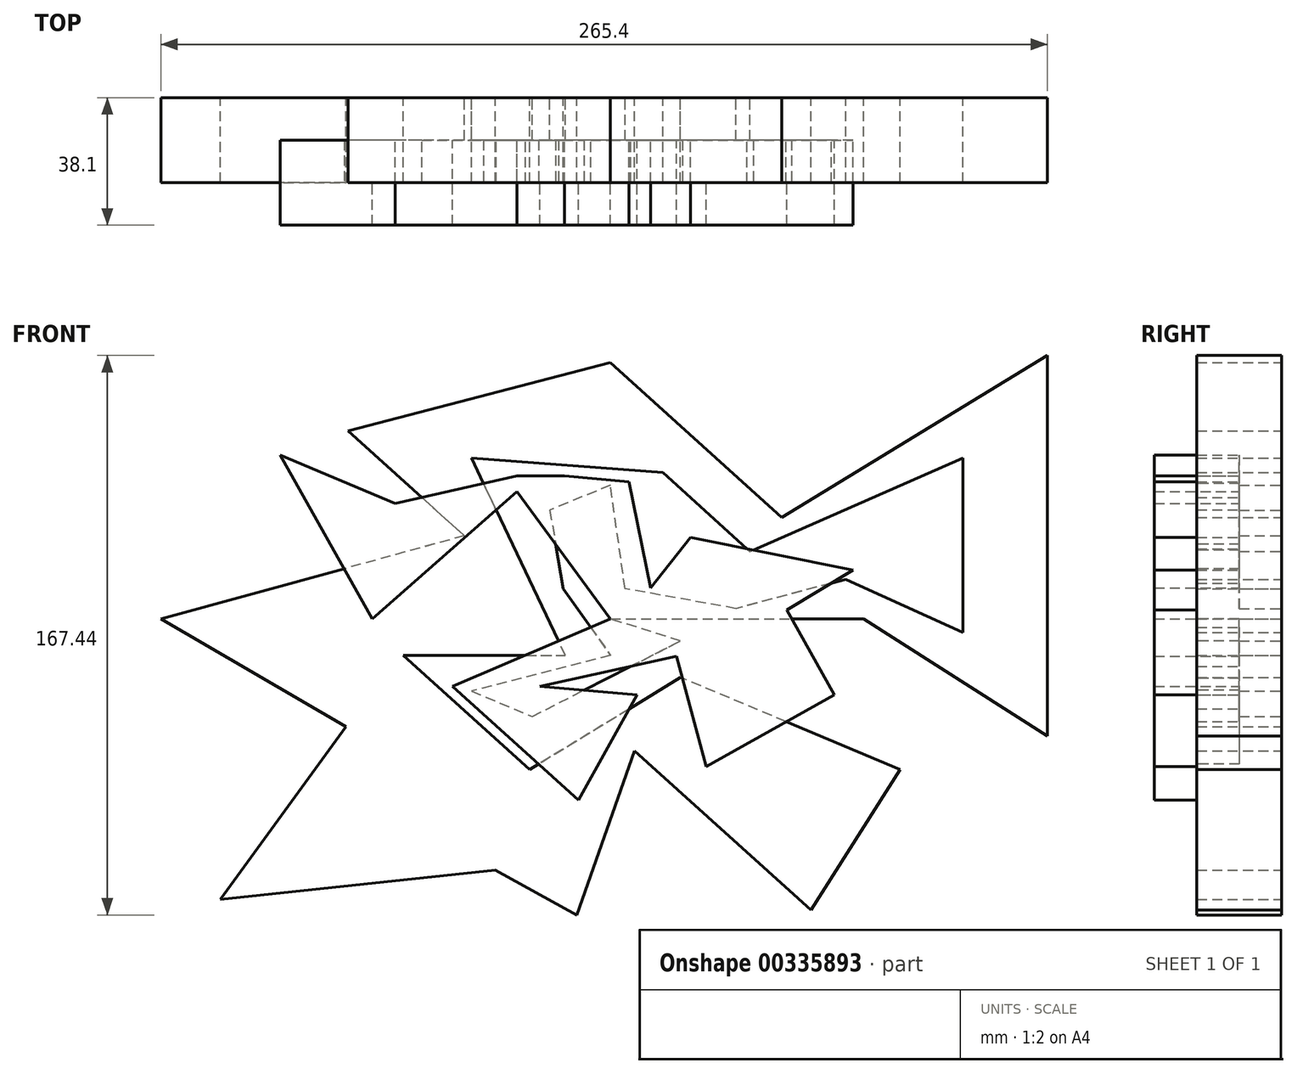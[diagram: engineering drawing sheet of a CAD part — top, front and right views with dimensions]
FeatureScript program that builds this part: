
annotation { "Feature Type Name" : "Feature", "Feature Type Description" : "" }
export const myFeature = defineFeature(function(context is Context, id is Id, definition is map)
    precondition{}
    {
        {
            var Q0;
            Q0=qCreatedBy(makeId("Front.planeOp"),FACE);
            var sketch = newSketch(context, id + "F0", { "sketchPlane" : qUnion([Q0])});
            skLineSegment(sketch, "E0", {"start": v(0, 0) * mm, "end": v(75.74, 0) * mm});
            skLineSegment(sketch, "E1", {"start": v(75.74, 0) * mm, "end": v(130.82, -35.05) * mm});
            skLineSegment(sketch, "E2", {"start": v(130.82, -35.05) * mm, "end": v(130.82, 78.87) * mm});
            skLineSegment(sketch, "E3", {"start": v(130.82, 78.87) * mm, "end": v(51.33, 30.36) * mm});
            skLineSegment(sketch, "E4", {"start": v(51.33, 30.36) * mm, "end": v(0, 76.68) * mm});
            skLineSegment(sketch, "E5", {"start": v(0, 76.68) * mm, "end": v(-78.56, 56.34) * mm});
            skLineSegment(sketch, "E6", {"start": v(-78.56, 56.34) * mm, "end": v(-43.72, 24.9) * mm});
            skLineSegment(sketch, "E7", {"start": v(-43.72, 24.9) * mm, "end": v(-134.58, 0) * mm});
            skLineSegment(sketch, "E8", {"start": v(-134.58, 0) * mm, "end": v(-79.18, -32.24) * mm});
            skLineSegment(sketch, "E9", {"start": v(-79.18, -32.24) * mm, "end": v(-116.74, -83.88) * mm});
            skLineSegment(sketch, "E10", {"start": v(-116.74, -83.88) * mm, "end": v(-34.43, -75.11) * mm});
            skLineSegment(sketch, "E11", {"start": v(-34.43, -75.11) * mm, "end": v(-10.02, -88.57) * mm});
            skLineSegment(sketch, "E12", {"start": v(-10.02, -88.57) * mm, "end": v(7.2, -39.43) * mm});
            skLineSegment(sketch, "E13", {"start": v(7.2, -39.43) * mm, "end": v(60, -87.08) * mm});
            skLineSegment(sketch, "E14", {"start": v(60, -87.08) * mm, "end": v(86.7, -45.07) * mm});
            skLineSegment(sketch, "E15", {"start": v(86.7, -45.07) * mm, "end": v(20.97, -17.53) * mm});
            skLineSegment(sketch, "E16", {"start": v(20.97, -17.53) * mm, "end": v(-24.1, -45.07) * mm});
            skLineSegment(sketch, "E17", {"start": v(-24.1, -45.07) * mm, "end": v(-61.99, -10.87) * mm});
            skLineSegment(sketch, "E18", {"start": v(-61.99, -10.87) * mm, "end": v(-13.46, -10.87) * mm});
            skLineSegment(sketch, "E19", {"start": v(-13.46, -10.87) * mm, "end": v(-41.63, 48.2) * mm});
            skLineSegment(sketch, "E20", {"start": v(-41.63, 48.2) * mm, "end": v(15.65, 43.82) * mm});
            skLineSegment(sketch, "E21", {"start": v(15.65, 43.82) * mm, "end": v(41.78, 20.23) * mm});
            skLineSegment(sketch, "E22", {"start": v(41.78, 20.23) * mm, "end": v(105.47, 48.2) * mm});
            skLineSegment(sketch, "E23", {"start": v(105.47, 48.2) * mm, "end": v(105.47, -4.07) * mm});
            skLineSegment(sketch, "E24", {"start": v(105.47, -4.07) * mm, "end": v(70.42, 11.9) * mm});
            skLineSegment(sketch, "E25", {"start": v(70.42, 11.9) * mm, "end": v(37.56, 3.13) * mm});
            skLineSegment(sketch, "E26", {"start": v(37.56, 3.13) * mm, "end": v(4.38, 9.08) * mm});
            skLineSegment(sketch, "E27", {"start": v(4.38, 9.08) * mm, "end": v(0, 40.06) * mm});
            skLineSegment(sketch, "E28", {"start": v(0, 40.06) * mm, "end": v(-18.15, 32.55) * mm});
            skLineSegment(sketch, "E29", {"start": v(-18.15, 32.55) * mm, "end": v(-14.08, 9.08) * mm});
            skLineSegment(sketch, "E30", {"start": v(-14.08, 9.08) * mm, "end": v(0, -10.87) * mm});
            skLineSegment(sketch, "E31", {"start": v(0, -10.87) * mm, "end": v(-41.63, -21.6) * mm});
            skLineSegment(sketch, "E32", {"start": v(-41.63, -21.6) * mm, "end": v(-23.46, -29.2) * mm});
            skLineSegment(sketch, "E33", {"start": v(-23.46, -29.2) * mm, "end": v(20.97, -6.57) * mm});
            skLineSegment(sketch, "E34", {"start": v(20.97, -6.57) * mm, "end": v(0, 0) * mm});
            skSolve(sketch);
        }
        {
            var Q0;
            Q0=makeQuery(id+"F0.imprint","IMPRINT",FACE,{"disambiguationData":[TD([[makeQuery(id+"F0.imprint","IMPRINT",EDGE,{"derivedFrom":sQuery(id+"F0.wireOp",EDGE,"E0")}),1.0]])]});
            extrude(context, id + "F1", {"entities" : qUnion([Q0]), "endBound" : BoundingType.SYMMETRIC, "depth" : 25.4 * mm});
        }
        {
            var Q0;
            Q0=qCreatedBy(makeId("Front.planeOp"),FACE);
            var sketch = newSketch(context, id + "F2", { "sketchPlane" : qUnion([Q0])});
            skLineSegment(sketch, "E35", {"start": v(-98.78, 49.06) * mm, "end": v(-71.26, 0) * mm});
            skLineSegment(sketch, "E36", {"start": v(-71.26, 0) * mm, "end": v(-27.97, 38.18) * mm});
            skLineSegment(sketch, "E37", {"start": v(-27.97, 38.18) * mm, "end": v(0, 0) * mm});
            skLineSegment(sketch, "E38", {"start": v(0, 0) * mm, "end": v(-47.28, -20.2) * mm});
            skLineSegment(sketch, "E39", {"start": v(-47.28, -20.2) * mm, "end": v(-9.55, -54.17) * mm});
            skLineSegment(sketch, "E40", {"start": v(-9.55, -54.17) * mm, "end": v(8, -22.64) * mm});
            skLineSegment(sketch, "E41", {"start": v(8, -22.64) * mm, "end": v(-21.09, -20.2) * mm});
            skLineSegment(sketch, "E42", {"start": v(-21.09, -20.2) * mm, "end": v(19.76, -11.1) * mm});
            skLineSegment(sketch, "E43", {"start": v(19.76, -11.1) * mm, "end": v(28.71, -44.15) * mm});
            skLineSegment(sketch, "E44", {"start": v(28.71, -44.15) * mm, "end": v(66.97, -22.69) * mm});
            skLineSegment(sketch, "E45", {"start": v(66.97, -22.69) * mm, "end": v(52.73, 2.7) * mm});
            skLineSegment(sketch, "E46", {"start": v(52.73, 2.7) * mm, "end": v(72.6, 14.65) * mm});
            skLineSegment(sketch, "E47", {"start": v(72.6, 14.65) * mm, "end": v(23.97, 24.42) * mm});
            skLineSegment(sketch, "E48", {"start": v(23.97, 24.42) * mm, "end": v(11.99, 9.32) * mm});
            skLineSegment(sketch, "E49", {"start": v(11.99, 9.32) * mm, "end": v(5.55, 41.07) * mm});
            skLineSegment(sketch, "E50", {"start": v(5.55, 41.07) * mm, "end": v(-13.76, 42.84) * mm});
            skLineSegment(sketch, "E51", {"start": v(-13.76, 42.84) * mm, "end": v(-27.97, 42.84) * mm});
            skLineSegment(sketch, "E52", {"start": v(-27.97, 42.84) * mm, "end": v(-64.38, 34.63) * mm});
            skLineSegment(sketch, "E53", {"start": v(-64.38, 34.63) * mm, "end": v(-98.78, 49.06) * mm});
            skSolve(sketch);
        }
        {
            var Q0;
            Q0 = qSketchRegion(id + "F2", true);
            extrude(context, id + "F3", {"entities" : qUnion([Q0]), "operationType" : NewBodyOperationType.ADD, "depth" : 25.4 * mm});
        }
    });
